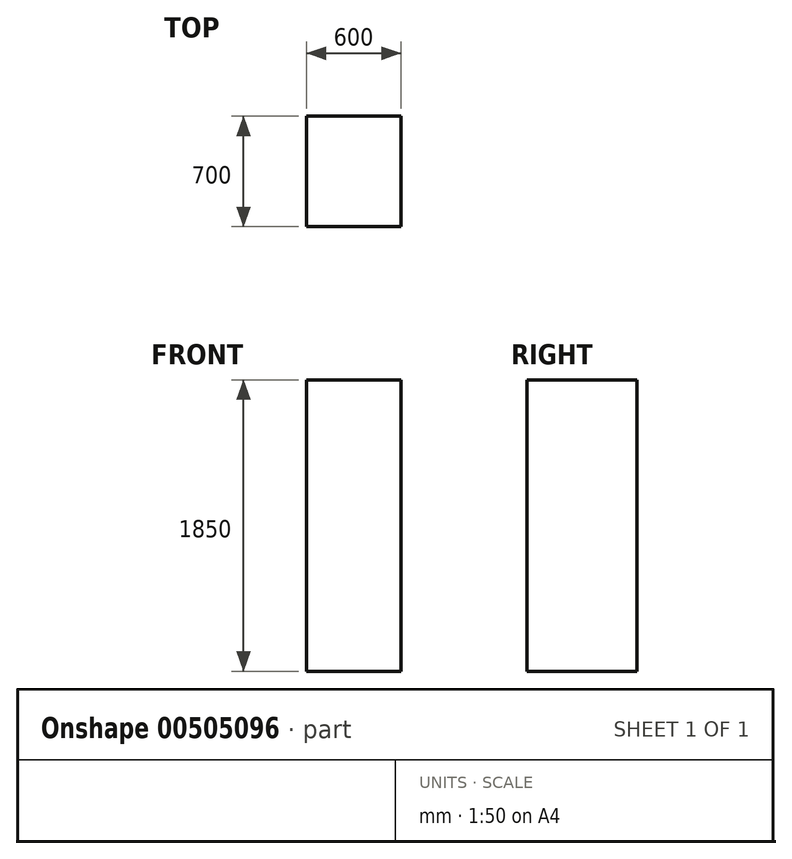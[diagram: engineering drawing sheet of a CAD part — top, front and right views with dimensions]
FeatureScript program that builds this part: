
annotation { "Feature Type Name" : "Feature", "Feature Type Description" : "" }
export const myFeature = defineFeature(function(context is Context, id is Id, definition is map)
    precondition{}
    {
        {
            var Q0;
            Q0=qCreatedBy(makeId("Top.planeOp"),FACE);
            var sketch = newSketch(context, id + "F0", { "sketchPlane" : qUnion([Q0])});
            skLineSegment(sketch, "E0.bottom", {"start": v(-320.15, 493.23) * mm, "end": v(279.85, 493.23) * mm});
            skLineSegment(sketch, "E0.top", {"start": v(-320.15, -206.77) * mm, "end": v(279.85, -206.77) * mm});
            skLineSegment(sketch, "E0.left", {"start": v(-320.15, 493.23) * mm, "end": v(-320.15, -206.77) * mm});
            skLineSegment(sketch, "E0.right", {"start": v(279.85, 493.23) * mm, "end": v(279.85, -206.77) * mm});
            skSolve(sketch);
        }
        {
            var Q0;
            Q0 = qSketchRegion(id + "F0", true);
            extrude(context, id + "F1", {"entities" : qUnion([Q0]), "depth" : 1850 * mm});
        }
    });
